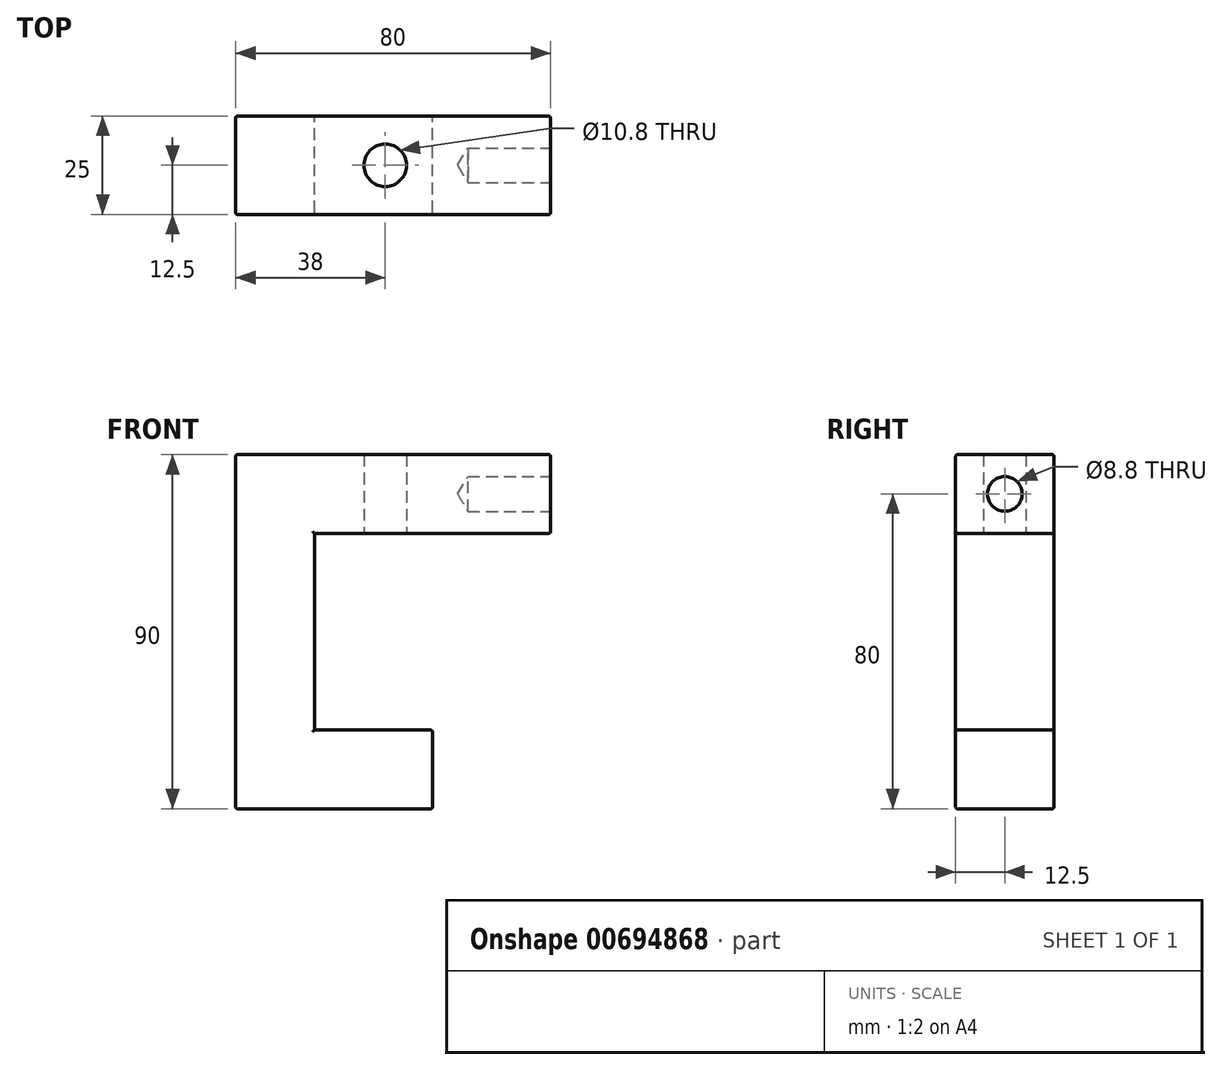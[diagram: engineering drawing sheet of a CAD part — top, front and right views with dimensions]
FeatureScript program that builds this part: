
annotation { "Feature Type Name" : "Feature", "Feature Type Description" : "" }
export const myFeature = defineFeature(function(context is Context, id is Id, definition is map)
    precondition{}
    {
        {
            var Q0;
            Q0=qCreatedBy(makeId("Front.planeOp"),FACE);
            var sketch = newSketch(context, id + "F0", { "sketchPlane" : qUnion([Q0])});
            skLineSegment(sketch, "E0", {"start": v(0, 0) * mm, "end": v(-30, 0) * mm});
            skLineSegment(sketch, "E1", {"start": v(-30, 0) * mm, "end": v(-30, 50) * mm});
            skLineSegment(sketch, "E2", {"start": v(-30, 50) * mm, "end": v(30, 50) * mm});
            skLineSegment(sketch, "E3", {"start": v(30, 50) * mm, "end": v(30, 70) * mm});
            skLineSegment(sketch, "E4", {"start": v(30, 70) * mm, "end": v(-50, 70) * mm});
            skLineSegment(sketch, "E5", {"start": v(-50, 70) * mm, "end": v(-50, -20) * mm});
            skLineSegment(sketch, "E6", {"start": v(-50, -20) * mm, "end": v(0, -20) * mm});
            skLineSegment(sketch, "E7", {"start": v(0, -20) * mm, "end": v(0, 0) * mm});
            skSolve(sketch);
        }
        {
            var Q0;
            Q0=makeQuery(id+"F0.imprint","IMPRINT",FACE,{"disambiguationData":[TD([[makeQuery(id+"F0.imprint","IMPRINT",EDGE,{"derivedFrom":sQuery(id+"F0.wireOp",EDGE,"E0")}),1.0]])]});
            extrude(context, id + "F1", {"entities" : qUnion([Q0]), "depth" : 25 * mm, "offsetDistance" : 25 * mm});
        }
        {
            var Q0;
            Q0=makeQuery(id+"F1.opExtrude","SWEPT_FACE",FACE,{"disambiguationData":[OSD([sQuery(id+"F0.wireOp",EDGE,"E2")])]});
            var sketch = newSketch(context, id + "F2", { "sketchPlane" : qUnion([Q0])});
            skPoint(sketch, "E8", {"position": v(-12, 12.5) * mm});
            skPoint(sketch, "E8.positionSnap0", {"position": v(30, 12.5) * mm});
            skSolve(sketch);
        }
        {
            var Q0;
            Q0=sQuery(id+"F2.wireOp",VERTEX,"E8");
            var Q1;
            Q1=makeQuery(id+"F1.opExtrude","SWEPT_BODY",BODY,{"disambiguationData":[OSD([sQuery(id+"F0.wireOp",EDGE,"E0"),sQuery(id+"F0.wireOp",EDGE,"E1"),sQuery(id+"F0.wireOp",EDGE,"E2"),sQuery(id+"F0.wireOp",EDGE,"E3"),sQuery(id+"F0.wireOp",EDGE,"E4"),sQuery(id+"F0.wireOp",EDGE,"E5"),sQuery(id+"F0.wireOp",EDGE,"E6"),sQuery(id+"F0.wireOp",EDGE,"E7")])]});
            hole(context, id + "F3", {"style" : HoleStyle.SIMPLE, "endStyle" : HoleEndStyle.BLIND, "standardTappedOrClearance" : lookupTablePath({ "standard" : "ISO", "engagement" : "75%", "pitch" : "1.25 mm", "size" : "M12", "type" : "Tapped" }), "standardBlindInLast" : lookupTablePath({ "standard" : "ISO", "engagement" : "75%", "pitch" : "1.25 mm", "size" : "M12", "type" : "Tapped" }), "holeDiameter" : 10.8 * mm, "majorDiameter" : 12 * mm, "showTappedDepth" : true, "holeDepth" : 21 * mm, "isTappedThrough" : true, "tappedDepth" : 17.25 * mm, "tapClearance" : 3, "locations" : qUnion([Q0]), "scope" : qUnion([Q1])});
        }
        {
            var Q0;
            Q0=makeQuery(id+"F1.opExtrude","SWEPT_FACE",FACE,{"disambiguationData":[OSD([sQuery(id+"F0.wireOp",EDGE,"E3")])]});
            var sketch = newSketch(context, id + "F4", { "sketchPlane" : qUnion([Q0])});
            skPoint(sketch, "E9", {"position": v(-12.5, 60) * mm});
            skPoint(sketch, "E9.positionSnap0", {"position": v(-12.5, 50) * mm});
            skPoint(sketch, "E9.positionSnap1", {"position": v(-25, 60) * mm});
            skSolve(sketch);
        }
        {
            var Q0;
            Q0=sQuery(id+"F4.wireOp",VERTEX,"E9");
            var Q1;
            Q1=makeQuery(id+"F1.opExtrude","SWEPT_BODY",BODY,{"disambiguationData":[OSD([sQuery(id+"F0.wireOp",EDGE,"E0"),sQuery(id+"F0.wireOp",EDGE,"E1"),sQuery(id+"F0.wireOp",EDGE,"E2"),sQuery(id+"F0.wireOp",EDGE,"E3"),sQuery(id+"F0.wireOp",EDGE,"E4"),sQuery(id+"F0.wireOp",EDGE,"E5"),sQuery(id+"F0.wireOp",EDGE,"E6"),sQuery(id+"F0.wireOp",EDGE,"E7")])]});
            hole(context, id + "F5", {"style" : HoleStyle.SIMPLE, "endStyle" : HoleEndStyle.BLIND, "standardTappedOrClearance" : lookupTablePath({ "standard" : "ISO", "engagement" : "75%", "pitch" : "1.25 mm", "size" : "M10", "type" : "Tapped" }), "standardBlindInLast" : lookupTablePath({ "standard" : "ISO", "engagement" : "75%", "pitch" : "1.25 mm", "size" : "M10", "type" : "Tapped" }), "holeDiameter" : 8.8 * mm, "majorDiameter" : 10 * mm, "showTappedDepth" : true, "holeDepth" : 21 * mm, "isTappedThrough" : true, "tappedDepth" : 17.25 * mm, "tapClearance" : 3, "locations" : qUnion([Q0]), "scope" : qUnion([Q1])});
        }
        {
            var Q0;
            Q0=makeQuery(id+"F1.opExtrude","CAP_FACE",FACE,{"disambiguationData":[OSD([sQuery(id+"F0.wireOp",EDGE,"E0"),sQuery(id+"F0.wireOp",EDGE,"E1"),sQuery(id+"F0.wireOp",EDGE,"E2"),sQuery(id+"F0.wireOp",EDGE,"E3"),sQuery(id+"F0.wireOp",EDGE,"E4"),sQuery(id+"F0.wireOp",EDGE,"E5"),sQuery(id+"F0.wireOp",EDGE,"E6"),sQuery(id+"F0.wireOp",EDGE,"E7")])],"isStart":false});
            var Q1;
            Q1=makeQuery(id+"F1.opExtrude","CAP_FACE",FACE,{"disambiguationData":[OSD([sQuery(id+"F0.wireOp",EDGE,"E0"),sQuery(id+"F0.wireOp",EDGE,"E1"),sQuery(id+"F0.wireOp",EDGE,"E2"),sQuery(id+"F0.wireOp",EDGE,"E3"),sQuery(id+"F0.wireOp",EDGE,"E4"),sQuery(id+"F0.wireOp",EDGE,"E5"),sQuery(id+"F0.wireOp",EDGE,"E6"),sQuery(id+"F0.wireOp",EDGE,"E7")])],"isStart":true});
            var Q2;
            Q2=makeQuery(id+"F1.opExtrude","SWEPT_EDGE",EDGE,{"disambiguationData":[OSD([sQuery(id+"F0.wireOp",EDGE,"E3"),sQuery(id+"F0.wireOp",EDGE,"E4")])]});
            var Q3;
            Q3=makeQuery(id+"F1.opExtrude","SWEPT_EDGE",EDGE,{"disambiguationData":[OSD([sQuery(id+"F0.wireOp",EDGE,"E2"),sQuery(id+"F0.wireOp",EDGE,"E3")])]});
            var Q4;
            Q4=makeQuery(id+"F1.opExtrude","SWEPT_EDGE",EDGE,{"disambiguationData":[OSD([sQuery(id+"F0.wireOp",EDGE,"E6"),sQuery(id+"F0.wireOp",EDGE,"E7")])]});
            var Q5;
            Q5=makeQuery(id+"F1.opExtrude","SWEPT_EDGE",EDGE,{"disambiguationData":[OSD([sQuery(id+"F0.wireOp",EDGE,"E0"),sQuery(id+"F0.wireOp",EDGE,"E7")])]});
            var Q6;
            Q6=makeQuery(id+"F1.opExtrude","SWEPT_EDGE",EDGE,{"disambiguationData":[OSD([sQuery(id+"F0.wireOp",EDGE,"E5"),sQuery(id+"F0.wireOp",EDGE,"E6")])]});
            var Q7;
            Q7=makeQuery(id+"F1.opExtrude","SWEPT_EDGE",EDGE,{"disambiguationData":[OSD([sQuery(id+"F0.wireOp",EDGE,"E4"),sQuery(id+"F0.wireOp",EDGE,"E5")])]});
            var Q8;
            Q8=makeQuery(id+"F5.hole-0.boolean.opBoolean","COPY",EDGE,{"derivedFrom":makeQuery(id+"F5.hole-0.opRevolve","SWEPT_EDGE",EDGE,{"disambiguationData":[OSD([sQuery(id+"F5.hole-0.sketch.wireOp",EDGE,"core_line_2"),sQuery(id+"F5.hole-0.sketch.wireOp",EDGE,"core_line_3")])]})});
            var Q9;
            Q9=makeQuery(id+"F3.hole-0.boolean.opBoolean","INTERSECT",EDGE,{"derivedFrom":[makeQuery(id+"F1.opExtrude","SWEPT_FACE",FACE,{"disambiguationData":[OSD([sQuery(id+"F0.wireOp",EDGE,"E4")])]}),makeQuery(id+"F3.hole-0.opRevolve","SWEPT_FACE",FACE,{"disambiguationData":[OSD([sQuery(id+"F3.hole-0.sketch.wireOp",EDGE,"core_line_2")])]})]});
            var Q10;
            Q10=makeQuery(id+"F3.hole-0.boolean.opBoolean","COPY",FACE,{"derivedFrom":makeQuery(id+"F3.hole-0.opRevolve","SWEPT_FACE",FACE,{"disambiguationData":[OSD([sQuery(id+"F3.hole-0.sketch.wireOp",EDGE,"core_line_2")])]})});
            fillet(context, id + "F6", {"entities" : qUnion([Q0, Q1, Q2, Q3, Q4, Q5, Q6, Q7, Q8, Q9, Q10]), "radius" : .5 * mm, "tangentPropagation" : true, "allowEdgeOverflow" : false});
        }
    });
